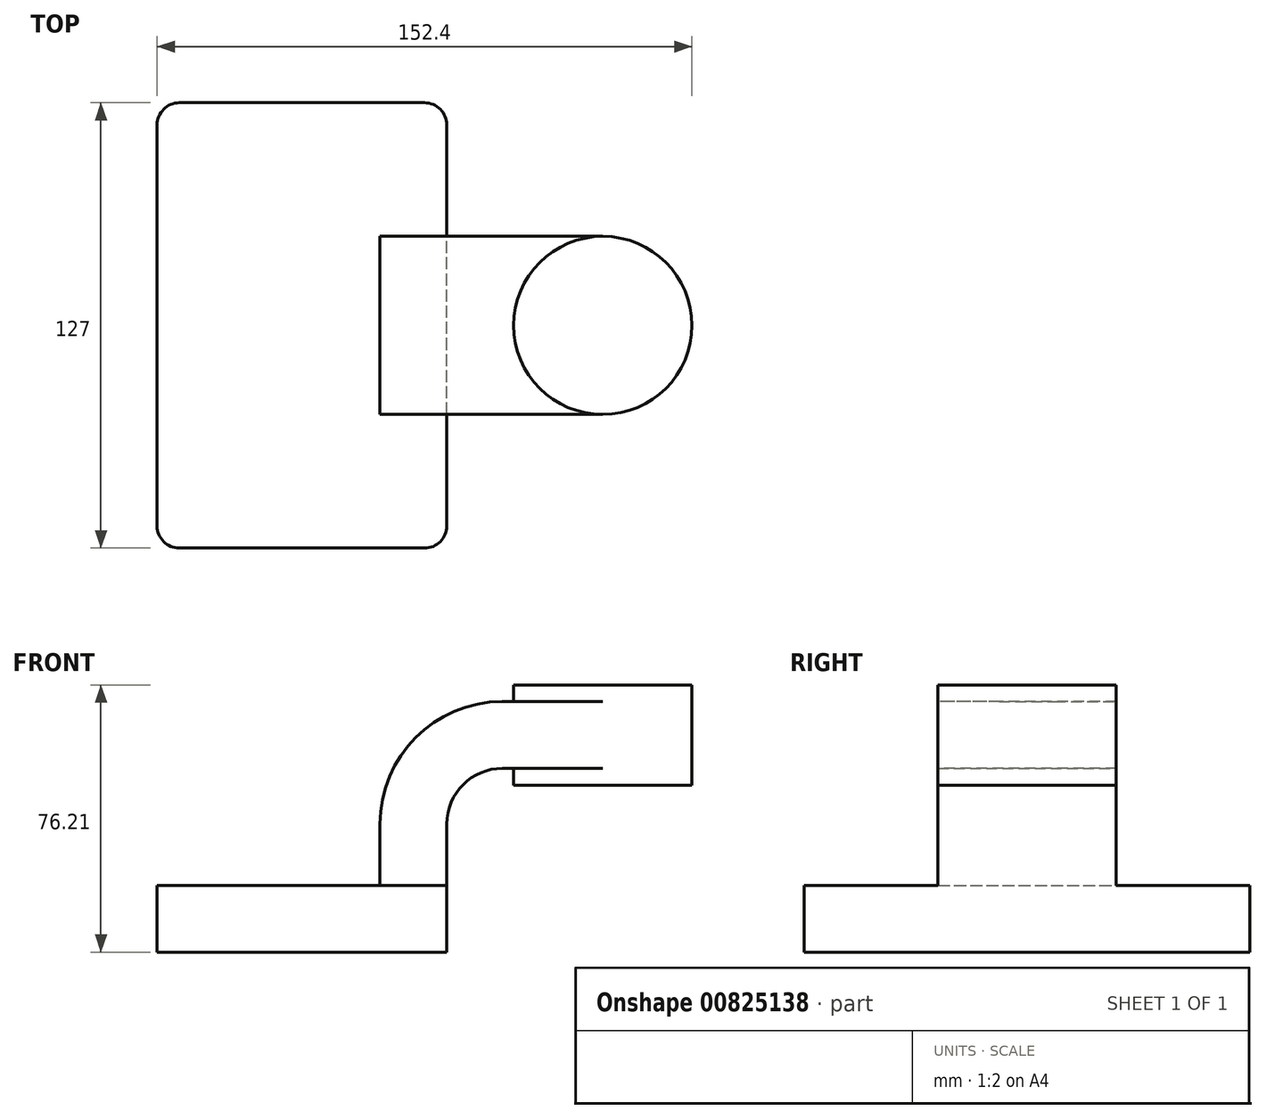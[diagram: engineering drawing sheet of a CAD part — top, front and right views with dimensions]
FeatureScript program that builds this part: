
annotation { "Feature Type Name" : "Feature", "Feature Type Description" : "" }
export const myFeature = defineFeature(function(context is Context, id is Id, definition is map)
    precondition{}
    {
        {
            var Q0;
            Q0=qCreatedBy(makeId("Front.planeOp"),FACE);
            var sketch = newSketch(context, id + "F0", { "sketchPlane" : qUnion([Q0])});
            skLineSegment(sketch, "E0.bottom", {"start": v(41.27, 9.53) * mm, "end": v(-41.28, 9.53) * mm});
            skLineSegment(sketch, "E0.top", {"start": v(41.28, -9.52) * mm, "end": v(-41.27, -9.52) * mm});
            skLineSegment(sketch, "E0.left", {"start": v(41.27, 9.53) * mm, "end": v(41.28, -9.52) * mm});
            skLineSegment(sketch, "E0.right", {"start": v(-41.28, 9.53) * mm, "end": v(-41.27, -9.52) * mm});
            skPoint(sketch, "E0.middle", {"position": v(0, 0) * mm});
            skLineSegment(sketch, "E1.bottom", {"start": v(111.13, 38.1) * mm, "end": v(60.33, 38.1) * mm});
            skLineSegment(sketch, "E1.top", {"start": v(111.13, 66.68) * mm, "end": v(60.33, 66.68) * mm});
            skLineSegment(sketch, "E1.left", {"start": v(111.13, 38.1) * mm, "end": v(111.13, 66.68) * mm});
            skLineSegment(sketch, "E1.right", {"start": v(60.33, 38.1) * mm, "end": v(60.33, 66.68) * mm});
            skPoint(sketch, "E1.middle", {"position": v(85.73, 52.39) * mm});
            skLineSegment(sketch, "E2", {"start": v(41.27, 9.53) * mm, "end": v(41.27, 27) * mm});
            skArc(sketch, "E3", {"start": v(41.27, 27) * mm, "mid": v(45.92, 38.23) * mm, "end": v(57.15, 42.88) * mm});
            skLineSegment(sketch, "E4", {"start": v(57.15, 42.88) * mm, "end": v(85.73, 42.88) * mm});
            skLineSegment(sketch, "E5.0", {"start": v(57.15, 61.93) * mm, "end": v(85.73, 61.93) * mm});
            skArc(sketch, "E5.1", {"start": v(22.22, 27) * mm, "mid": v(32.45, 51.7) * mm, "end": v(57.15, 61.93) * mm});
            skLineSegment(sketch, "E5.2", {"start": v(22.22, 9.53) * mm, "end": v(22.22, 27) * mm});
            skLineSegment(sketch, "E6", {"start": v(85.73, 66.68) * mm, "end": v(85.73, 38.1) * mm});
            skFitSpline(sketch, "E7", {"points": [v(-41.28, 9.53) * mm, v(57.15, 61.93) * mm], "startDerivative": vector(1.77, 91.6) * mm, "endDerivative": vector(133.72, 0.23) * mm});
            skSolve(sketch);
        }
        {
            var Q0;
            Q0=makeQuery(id+"F0.imprint","IMPRINT",FACE,{"disambiguationData":[TD([[makeQuery(id+"F0.imprint","IMPRINT",EDGE,{"derivedFrom":sQuery(id+"F0.wireOp",EDGE,"E0.top")}),-1.0]])]});
            extrude(context, id + "F1", {"entities" : qUnion([Q0]), "endBound" : BoundingType.SYMMETRIC, "depth" : 127 * mm, "offsetDistance" : 25.4 * mm});
        }
        {
            var Q0;
            {var subQ5=sQuery(id+"F0.wireOp",EDGE,"E2");Q0=makeQuery(id+"F0.imprint","IMPRINT",FACE,{"disambiguationData":[TD([[makeQuery(id+"F0.imprint","IMPRINT",EDGE,{"derivedFrom":subQ5}),1.0]])]});}
            var Q1;
            {var subQ0=sQuery(id+"F0.wireOp",EDGE,"E4");var subQ1=sQuery(id+"F0.wireOp",EDGE,"E1.right");var subQ2=makeQuery(id+"F0.imprint","INTERSECT",VERTEX,{"derivedFrom":[subQ1,subQ0]});Q1=makeQuery(id+"F0.imprint","IMPRINT",FACE,{"disambiguationData":[TD([[makeQuery(id+"F0.imprint","IMPRINT",EDGE,{"disambiguationData":[TD([[subQ2,-1.0]])],"derivedFrom":subQ1}),-1.0]])]});}
            extrude(context, id + "F2", {"entities" : qUnion([Q0, Q1]), "operationType" : NewBodyOperationType.ADD, "endBound" : BoundingType.SYMMETRIC, "depth" : 50.8 * mm, "offsetDistance" : 25.4 * mm});
        }
        {
            var Q0;
            {var subQ4=sQuery(id+"F0.wireOp",EDGE,"E5.1");Q0=makeQuery(id+"F0.imprint","IMPRINT",FACE,{"disambiguationData":[TD([[makeQuery(id+"F0.imprint","IMPRINT",EDGE,{"derivedFrom":subQ4}),1.0]])]});}
            extrude(context, id + "F3", {"entities" : qUnion([Q0]), "operationType" : NewBodyOperationType.ADD, "endBound" : BoundingType.SYMMETRIC, "depth" : 15.88 * mm, "offsetDistance" : 25.4 * mm});
        }
        {
            var Q0;
            {var subQ4=sQuery(id+"F0.wireOp",EDGE,"E1.left");Q0=makeQuery(id+"F0.imprint","IMPRINT",FACE,{"disambiguationData":[TD([[makeQuery(id+"F0.imprint","IMPRINT",EDGE,{"derivedFrom":subQ4}),1.0]])]});}
            var Q1;
            Q1=sQuery(id+"F0.wireOp",EDGE,"E6");
            revolve(context, id + "F4", {"operationType" : NewBodyOperationType.ADD, "surfaceOperationType" : NewSurfaceOperationType.NEW, "entities" : qUnion([Q0]), "axis" : qUnion([Q1]), "revolveType" : RevolveType.FULL});
        }
        {
            var Q0;
            Q0=makeQuery(id+"F1.opExtrude","CAP_EDGE",EDGE,{"disambiguationData":[OSD([sQuery(id+"F0.wireOp",EDGE,"E0.right")])],"isStart":false});
            var Q1;
            Q1=makeQuery(id+"F1.opExtrude","CAP_EDGE",EDGE,{"disambiguationData":[OSD([sQuery(id+"F0.wireOp",EDGE,"E0.left")])],"isStart":false});
            var Q2;
            Q2=makeQuery(id+"F1.opExtrude","CAP_EDGE",EDGE,{"disambiguationData":[OSD([sQuery(id+"F0.wireOp",EDGE,"E0.left")])],"isStart":true});
            var Q3;
            Q3=makeQuery(id+"F1.opExtrude","CAP_EDGE",EDGE,{"disambiguationData":[OSD([sQuery(id+"F0.wireOp",EDGE,"E0.right")])],"isStart":true});
            fillet(context, id + "F5", {"entities" : qUnion([Q0, Q1, Q2, Q3]), "radius" : 6.35 * mm, "tangentPropagation" : true, "allowEdgeOverflow" : false});
        }
    });
